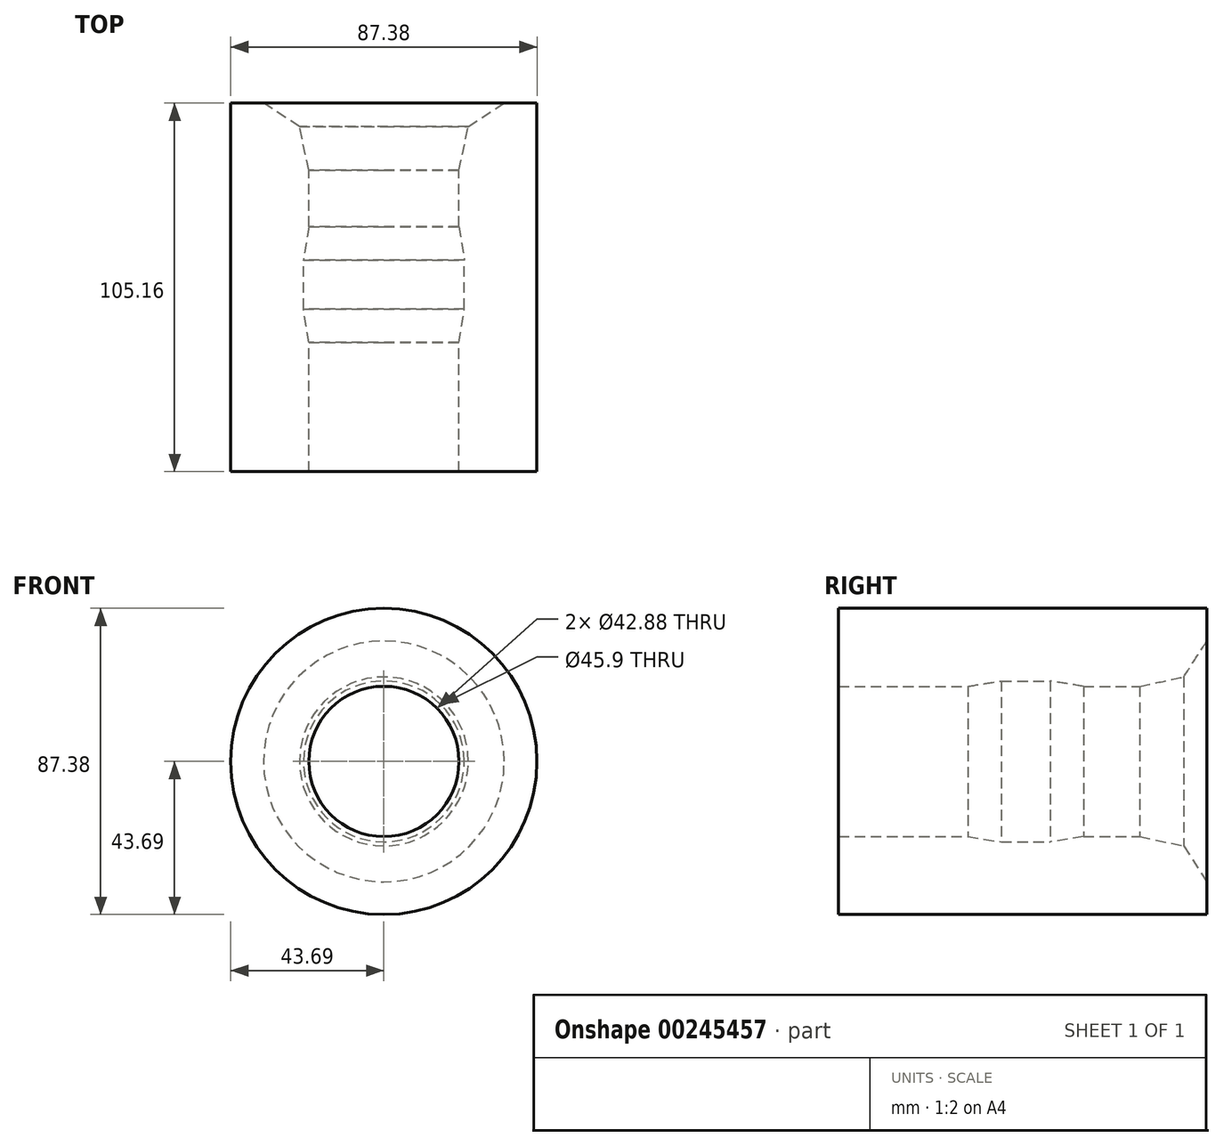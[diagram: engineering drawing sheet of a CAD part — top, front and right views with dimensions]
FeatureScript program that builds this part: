
annotation { "Feature Type Name" : "Feature", "Feature Type Description" : "" }
export const myFeature = defineFeature(function(context is Context, id is Id, definition is map)
    precondition{}
    {
        {
            var Q0;
            Q0=qCreatedBy(makeId("Right.planeOp"),FACE);
            var sketch = newSketch(context, id + "F0", { "sketchPlane" : qUnion([Q0])});
            skLineSegment(sketch, "E0", {"start": v(-105.16, 21.44) * mm, "end": v(-68.28, 21.44) * mm});
            skLineSegment(sketch, "E1", {"start": v(-35.26, 21.44) * mm, "end": v(-19.2, 21.44) * mm});
            skLineSegment(sketch, "E2", {"start": v(-19.2, 21.44) * mm, "end": v(-6.65, 24.1) * mm});
            skLineSegment(sketch, "E3", {"start": v(-6.65, 24.1) * mm, "end": v(0, 34.35) * mm});
            skLineSegment(sketch, "E4.trimOffspring", {"start": v(0, 34.35) * mm, "end": v(0, 43.69) * mm});
            skLineSegment(sketch, "E5", {"start": v(0, 43.69) * mm, "end": v(-105.16, 43.69) * mm});
            skLineSegment(sketch, "E6", {"start": v(-68.28, 21.44) * mm, "end": v(-58.73, 22.95) * mm});
            skPoint(sketch, "E7", {"position": v(-35.26, 21.44) * mm});
            skLineSegment(sketch, "E8", {"start": v(-35.26, 21.44) * mm, "end": v(-44.8, 22.95) * mm});
            skLineSegment(sketch, "E9.trimOffspring", {"start": v(-58.73, 22.95) * mm, "end": v(-44.8, 22.95) * mm});
            skLineSegment(sketch, "E10", {"start": v(-105.16, 43.69) * mm, "end": v(-105.16, 21.44) * mm});
            skLineSegment(sketch, "E11", {"start": v(0, 0) * mm, "end": v(-112.9, 0) * mm});
            skSolve(sketch);
        }
        {
            var Q0;
            Q0=makeQuery(id+"F0.imprint","IMPRINT",FACE,{"disambiguationData":[TD([[makeQuery(id+"F0.imprint","IMPRINT",EDGE,{"derivedFrom":sQuery(id+"F0.wireOp",EDGE,"E0")}),1.0]])]});
            var Q1;
            Q1=sQuery(id+"F0.wireOp",EDGE,"E11");
            revolve(context, id + "F1", {"entities" : qUnion([Q0]), "axis" : qUnion([Q1]), "revolveType" : RevolveType.FULL});
        }
    });
